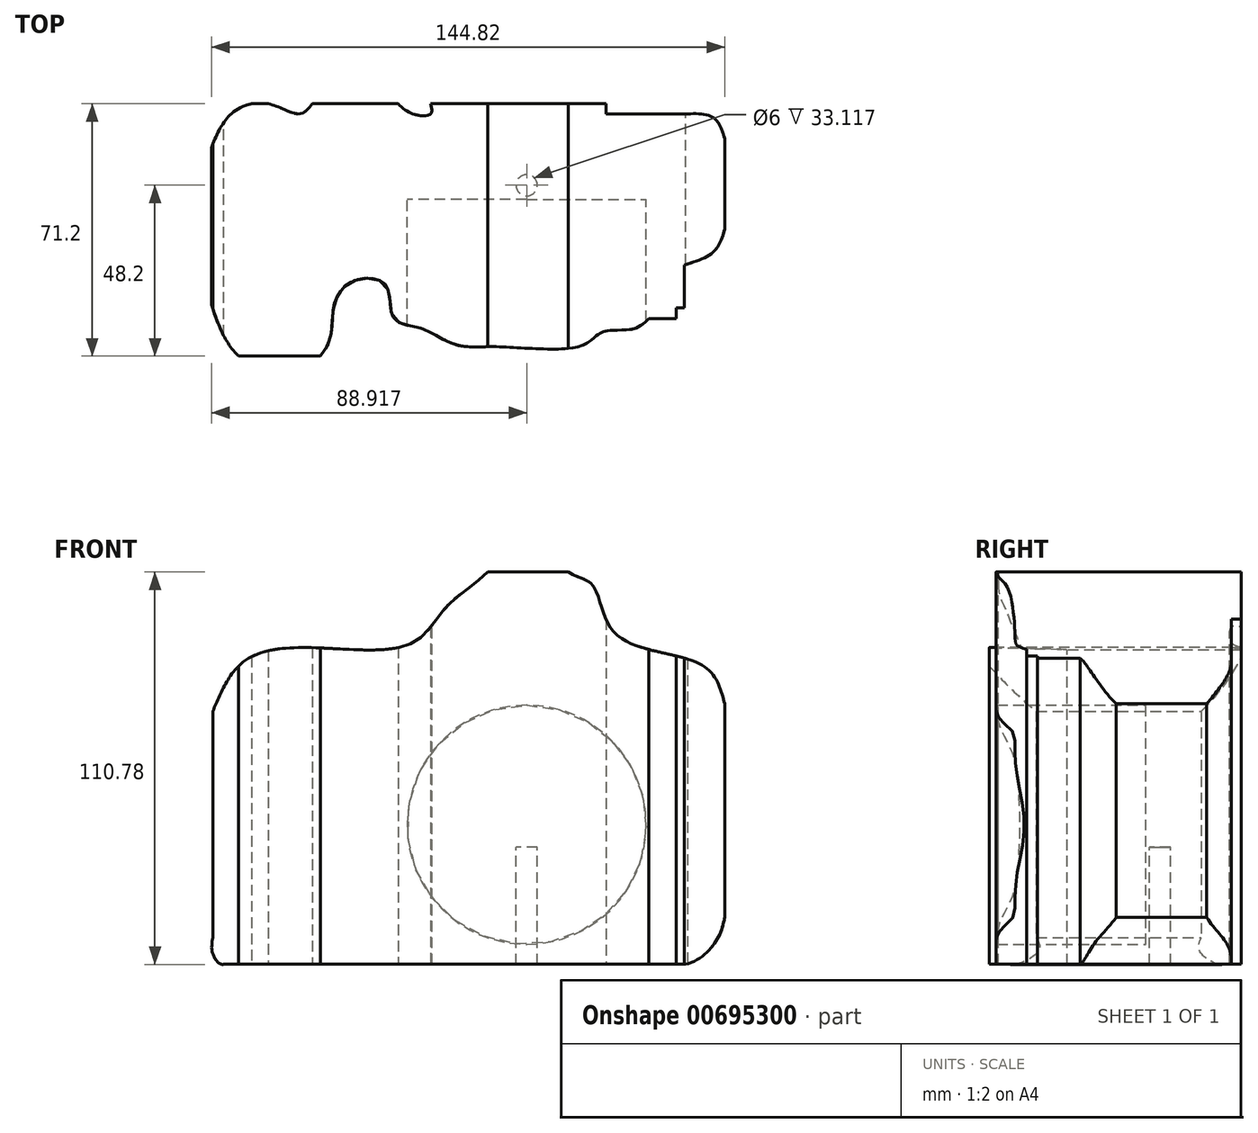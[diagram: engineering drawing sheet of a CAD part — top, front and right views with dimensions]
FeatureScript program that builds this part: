
annotation { "Feature Type Name" : "Feature", "Feature Type Description" : "" }
export const myFeature = defineFeature(function(context is Context, id is Id, definition is map)
    precondition{}
    {
        {
            var Q0;
            Q0=qCreatedBy(makeId("Front.planeOp"),FACE);
            var sketch = newSketch(context, id + "F0", { "sketchPlane" : qUnion([Q0])});
            skLineSegment(sketch, "E0", {"start": v(-74.31, -25.52) * mm, "end": v(-74.31, 38.34) * mm});
            skLineSegment(sketch, "E1", {"start": v(-71.29, -33.12) * mm, "end": v(59.1, -33.12) * mm});
            skLineSegment(sketch, "E2", {"start": v(70.19, -19.9) * mm, "end": v(70.19, 40.48) * mm});
            skLineSegment(sketch, "E3", {"start": v(3.26, 77.63) * mm, "end": v(25.97, 77.63) * mm});
            skFitSpline(sketch, "E4", {"points": [v(25.97, 77.63) * mm, v(32.92, 73.88) * mm, v(39.6, 59.99) * mm, v(63.65, 51.44) * mm, v(70.19, 40.48) * mm], "startDerivative": vector(40.41, -26.82) * mm, "endDerivative": vector(14.83, -55.3) * mm});
            skFitSpline(sketch, "E5", {"points": [v(70.19, -19.9) * mm, v(67.4, -27.12) * mm, v(59.1, -33.12) * mm], "startDerivative": vector(-3.3, -17.11) * mm, "endDerivative": vector(-18.7, -3.49) * mm});
            skFitSpline(sketch, "E6", {"points": [v(-71.29, -33.12) * mm, v(-74.31, -30.13) * mm, v(-74.31, -25.52) * mm], "startDerivative": vector(-8.27, -1.87) * mm, "endDerivative": vector(1.87, 10.66) * mm});
            skFitSpline(sketch, "E7", {"points": [v(-74.31, 38.34) * mm, v(-65.41, 52.5) * mm, v(-45.37, 56.25) * mm, v(-18.11, 57.58) * mm, v(-8.23, 68) * mm, v(3.26, 77.63) * mm], "startDerivative": vector(37.04, 88.06) * mm, "endDerivative": vector(65.2, 64.85) * mm});
            skCircle(sketch, "E8", {"center": v(14.29, 6.28) * mm, "radius": 33.75 * mm});
            skSolve(sketch);
        }
        {
            var Q0;
            Q0 = qSketchRegion(id + "F0", true);
            var Q1;
            Q1=makeQuery(id+"F0.imprint","IMPRINT",FACE,{"disambiguationData":[TD([[makeQuery(id+"F0.imprint","IMPRINT",EDGE,{"derivedFrom":sQuery(id+"F0.wireOp",EDGE,"E8")}),1.0]])]});
            extrude(context, id + "F1", {"entities" : qUnion([Q0, Q1]), "depth" : 71.2 * mm, "offsetDistance" : 25 * mm});
        }
        {
            var Q0;
            Q0=makeQuery(id+"F0.imprint","IMPRINT",FACE,{"disambiguationData":[TD([[makeQuery(id+"F0.imprint","IMPRINT",EDGE,{"derivedFrom":sQuery(id+"F0.wireOp",EDGE,"E8")}),1.0]])]});
            extrude(context, id + "F2", {"entities" : qUnion([Q0]), "depth" : 114 * mm, "offsetDistance" : 25 * mm, "hasSecondDirection" : true, "secondDirectionOppositeDirection" : false, "secondDirectionDepth" : 27 * mm});
        }
        {
            var Q0;
            Q0=qCreatedBy(makeId("Top.planeOp"),FACE);
            var sketch = newSketch(context, id + "F3", { "sketchPlane" : qUnion([Q0])});
            skLineSegment(sketch, "E9", {"start": v(-75.62, -53.78) * mm, "end": v(-75.62, -14.69) * mm});
            skLineSegment(sketch, "E10", {"start": v(-46.3, 0) * mm, "end": v(-22, 0) * mm});
            skLineSegment(sketch, "E11", {"start": v(-12.83, 0) * mm, "end": v(36.64, 0) * mm});
            skLineSegment(sketch, "E12", {"start": v(36.64, 0) * mm, "end": v(36.64, -2.84) * mm});
            skLineSegment(sketch, "E13", {"start": v(36.64, -2.84) * mm, "end": v(59.74, -2.84) * mm});
            skLineSegment(sketch, "E14", {"start": v(70.7, -11.72) * mm, "end": v(70.7, -33.05) * mm});
            skLineSegment(sketch, "E15", {"start": v(58.85, -45.5) * mm, "end": v(58.85, -57.63) * mm});
            skLineSegment(sketch, "E16", {"start": v(58.85, -57.63) * mm, "end": v(56.48, -57.63) * mm});
            skLineSegment(sketch, "E17", {"start": v(56.48, -57.63) * mm, "end": v(56.48, -60.6) * mm});
            skLineSegment(sketch, "E18", {"start": v(56.48, -60.6) * mm, "end": v(48.78, -60.6) * mm});
            skFitSpline(sketch, "E19", {"points": [v(-75.62, -53.78) * mm, v(-67.62, -70.67) * mm, v(-53.1, -76.23) * mm, v(-41.85, -68) * mm, v(-40.08, -56.75) * mm, v(-34.45, -49.93) * mm, v(-25.56, -51.12) * mm, v(-23.49, -60) * mm, v(-18.75, -62.67) * mm, v(-14.3, -63.86) * mm, v(-5.72, -68) * mm, v(5.83, -68.6) * mm, v(29.83, -68.3) * mm, v(35.75, -64.45) * mm, v(44.34, -63.56) * mm, v(48.78, -60.6) * mm], "startDerivative": vector(64.78, -209.55) * mm, "endDerivative": vector(76.94, 77.45) * mm});
            skFitSpline(sketch, "E20", {"points": [v(58.85, -45.5) * mm, v(67.44, -41.34) * mm, v(70.7, -33.05) * mm], "startDerivative": vector(19.5, 5.94) * mm, "endDerivative": vector(4.1, 19.02) * mm});
            skFitSpline(sketch, "E21", {"points": [v(70.7, -11.72) * mm, v(67.15, -4.02) * mm, v(59.74, -2.84) * mm], "startDerivative": vector(-4.74, 18.16) * mm, "endDerivative": vector(-17.31, -0.58) * mm});
            skFitSpline(sketch, "E22", {"points": [v(-12.83, 0) * mm, v(-12.83, -2.84) * mm, v(-17.86, -2.84) * mm, v(-22, 0) * mm], "startDerivative": vector(3.34, -12.35) * mm, "endDerivative": vector(-9.7, 9.12) * mm});
            skFitSpline(sketch, "E23", {"points": [v(-46.3, 0) * mm, v(-49.85, -2.84) * mm, v(-58.74, 0) * mm, v(-69.1, -2.84) * mm, v(-75.62, -14.69) * mm], "startDerivative": vector(-17.28, -23.13) * mm, "endDerivative": vector(-16.85, -44.86) * mm});
            skSolve(sketch);
        }
        {
            var Q0;
            Q0 = qSketchRegion(id + "F3", true);
            extrude(context, id + "F4", {"entities" : qUnion([Q0]), "operationType" : NewBodyOperationType.INTERSECT, "endBound" : BoundingType.SYMMETRIC, "depth" : 200 * mm, "offsetDistance" : 25 * mm});
        }
        {
            var Q0;
            Q0=qCreatedBy(makeId("Top.planeOp"),FACE);
            var sketch = newSketch(context, id + "F5", { "sketchPlane" : qUnion([Q0])});
            skCircle(sketch, "E24", {"center": v(14.29, -23) * mm, "radius": 3 * mm});
            skPoint(sketch, "E25.0", {"position": v(14.29, 0) * mm});
            skSolve(sketch);
        }
        {
            var Q0;
            Q0=makeQuery(id+"F5.imprint","IMPRINT",FACE,{"disambiguationData":[TD([[makeQuery(id+"F5.imprint","IMPRINT",EDGE,{"derivedFrom":sQuery(id+"F5.wireOp",EDGE,"E24")}),1.0]])]});
            var Q1;
            Q1=sQuery(id+"F5.wireOp",EDGE,"E24");
            extrude(context, id + "F6", {"entities" : qUnion([Q0]), "operationType" : NewBodyOperationType.REMOVE, "surfaceEntities" : qUnion([Q1]), "oppositeDirection" : true, "depth" : 46 * mm, "offsetDistance" : 25 * mm});
        }
    });
